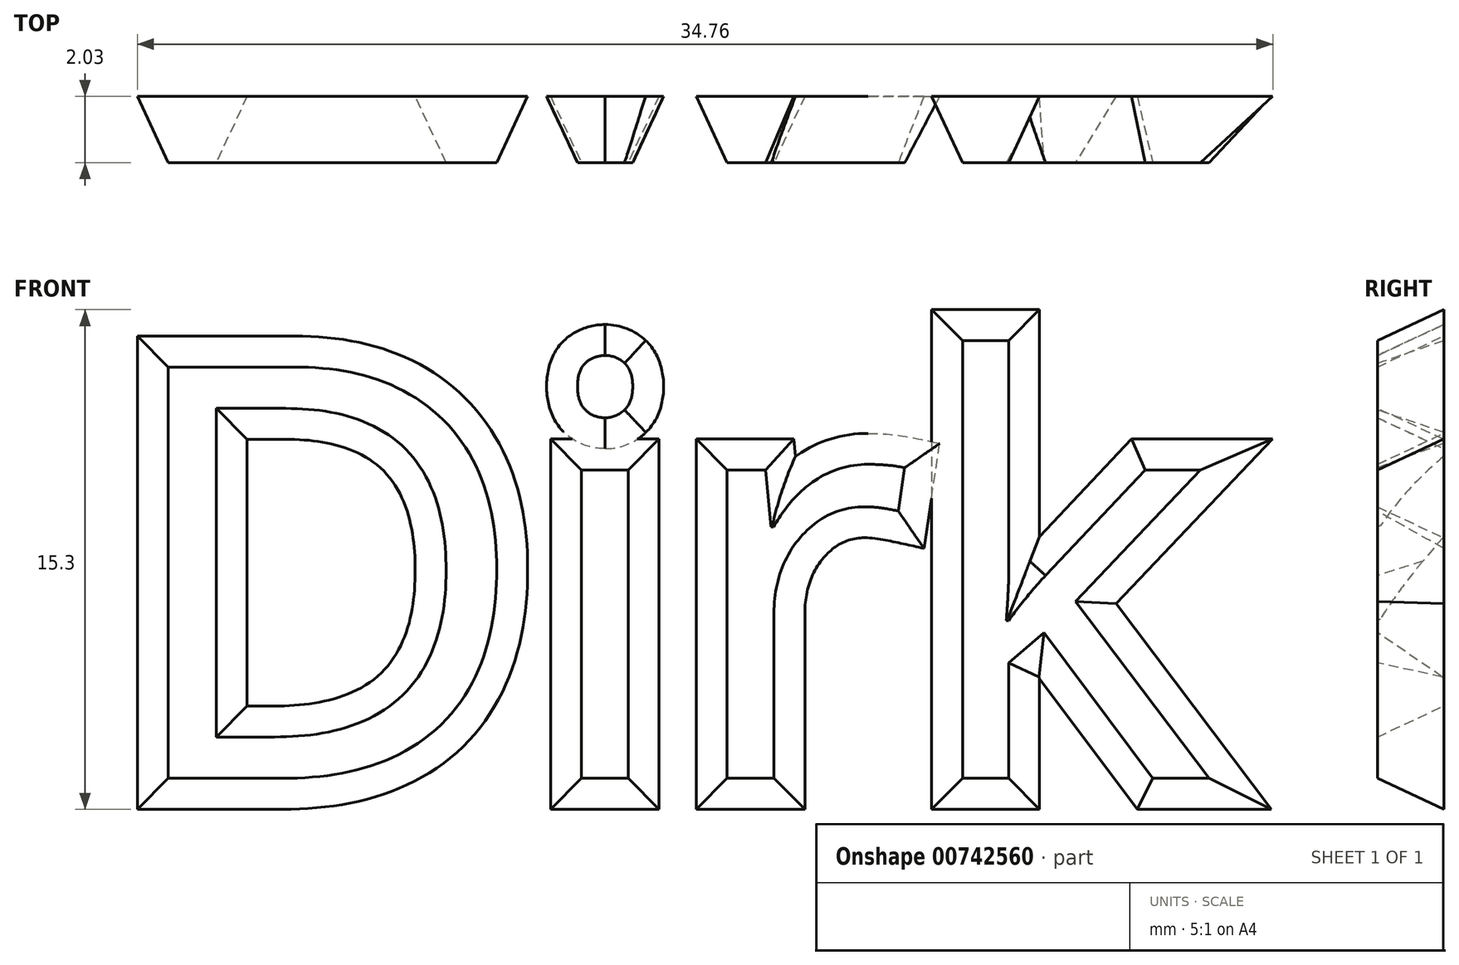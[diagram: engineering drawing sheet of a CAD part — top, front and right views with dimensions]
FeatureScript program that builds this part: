
annotation { "Feature Type Name" : "Feature", "Feature Type Description" : "" }
export const myFeature = defineFeature(function(context is Context, id is Id, definition is map)
    precondition{}
    {
        {
            var Q0;
            Q0=qCreatedBy(makeId("Front.planeOp"),FACE);
            var sketch = newSketch(context, id + "F0", { "sketchPlane" : qUnion([Q0])});
            skPoint(sketch, "E0.middle", {"position": v(0, 0) * mm});
            skText(sketch, "E1", { "text": "Dirk", "fontName": "OpenSans-Regular.ttf"});
            const initialGuessF0  = {"E1": [-0.01737, -0.0127, 1, 0, 0.0127]};
            skSetInitialGuess(sketch, initialGuessF0);
            skSolve(sketch);
        }
        {
            var Q0;
            Q0 = qSketchRegion(id + "F0", true);
            extrude(context, id + "F1", {"entities" : qUnion([Q0]), "oppositeDirection" : true, "depth" : 2.03 * mm, "offsetDistance" : 25.4 * mm, "hasDraft" : true, "draftAngle" : 25 * degree});
        }
    });
